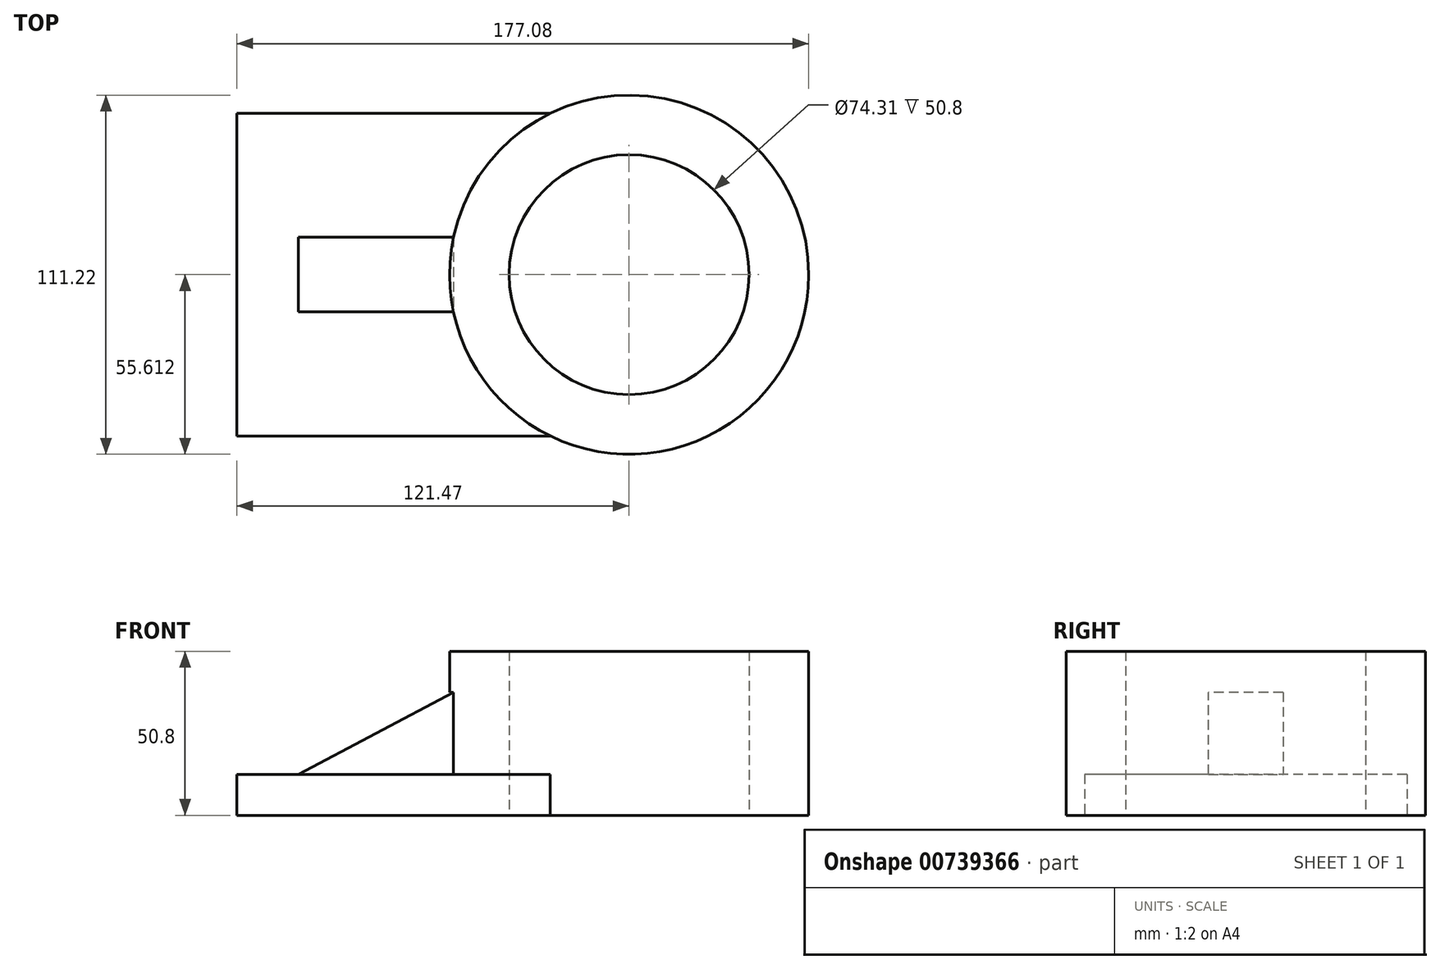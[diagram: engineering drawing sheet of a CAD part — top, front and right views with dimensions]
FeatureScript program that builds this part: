
annotation { "Feature Type Name" : "Feature", "Feature Type Description" : "" }
export const myFeature = defineFeature(function(context is Context, id is Id, definition is map)
    precondition{}
    {
        {
            var Q0;
            Q0=qCreatedBy(makeId("Top.planeOp"),FACE);
            var sketch = newSketch(context, id + "F0", { "sketchPlane" : qUnion([Q0])});
            skLineSegment(sketch, "E0.bottom", {"start": v(-73.9, 65.56) * mm, "end": v(23.08, 65.56) * mm});
            skLineSegment(sketch, "E0.top", {"start": v(-73.9, -34.3) * mm, "end": v(23.08, -34.3) * mm});
            skLineSegment(sketch, "E0.left", {"start": v(-73.9, 65.56) * mm, "end": v(-73.9, -34.3) * mm});
            skCircle(sketch, "E1", {"center": v(47.56, 15.63) * mm, "radius": 55.6 * mm});
            skPoint(sketch, "E1.third.point", {"position": v(92.68, -16.87) * mm});
            skCircle(sketch, "E2", {"center": v(47.56, 15.63) * mm, "radius": 37.16 * mm});
            skSolve(sketch);
        }
        {
            var Q0;
            {var subQ0=sQuery(id+"F0.wireOp",EDGE,"E0.bottom");Q0=makeQuery(id+"F0.imprint","IMPRINT",FACE,{"disambiguationData":[TD([[makeQuery(id+"F0.imprint","IMPRINT",EDGE,{"derivedFrom":subQ0}),-1.0]])]});}
            extrude(context, id + "F1", {"entities" : qUnion([Q0]), "depth" : 12.7 * mm, "offsetDistance" : 25.4 * mm});
        }
        {
            var Q0;
            Q0=makeQuery(id+"F0.imprint","IMPRINT",FACE,{"disambiguationData":[TD([[makeQuery(id+"F0.imprint","IMPRINT",EDGE,{"derivedFrom":sQuery(id+"F0.wireOp",EDGE,"E2")}),-1.0]])]});
            extrude(context, id + "F2", {"entities" : qUnion([Q0]), "operationType" : NewBodyOperationType.ADD, "depth" : 50.8 * mm, "offsetDistance" : 25.4 * mm});
        }
        {
            var Q0;
            Q0=qCreatedBy(makeId("Top.planeOp"),FACE);
            var sketch = newSketch(context, id + "F3", { "sketchPlane" : qUnion([Q0])});
            skLineSegment(sketch, "E3.bottom", {"start": v(-54.86, 27.24) * mm, "end": v(7.6, 27.24) * mm});
            skLineSegment(sketch, "E3.top", {"start": v(-54.86, 4.08) * mm, "end": v(7.6, 4.08) * mm});
            skLineSegment(sketch, "E3.left", {"start": v(-54.86, 27.24) * mm, "end": v(-54.86, 4.08) * mm});
            skLineSegment(sketch, "E3.right", {"start": v(7.6, 27.24) * mm, "end": v(7.6, 4.08) * mm});
            skSolve(sketch);
        }
        {
            var Q0;
            Q0=makeQuery(id+"F3.imprint","IMPRINT",FACE,{"disambiguationData":[TD([[makeQuery(id+"F3.imprint","IMPRINT",EDGE,{"derivedFrom":sQuery(id+"F3.wireOp",EDGE,"E3.bottom")}),-1.0]])]});
            extrude(context, id + "F4", {"entities" : qUnion([Q0]), "operationType" : NewBodyOperationType.ADD, "depth" : 38.1 * mm, "offsetDistance" : 25.4 * mm});
        }
        {
            var Q0;
            Q0=makeQuery(id+"F4.opExtrude","SWEPT_FACE",FACE,{"disambiguationData":[OSD([sQuery(id+"F3.wireOp",EDGE,"E3.top")])]});
            var sketch = newSketch(context, id + "F5", { "sketchPlane" : qUnion([Q0])});
            skLineSegment(sketch, "E4", {"start": v(-54.86, 12.7) * mm, "end": v(-6.83, 38.1) * mm});
            skLineSegment(sketch, "E5", {"start": v(-6.83, 38.1) * mm, "end": v(-54.86, 38.1) * mm});
            skLineSegment(sketch, "E6", {"start": v(-54.86, 38.1) * mm, "end": v(-54.86, 12.7) * mm});
            skSolve(sketch);
        }
        {
            var Q0;
            Q0=makeQuery(id+"F5.imprint","IMPRINT",FACE,{"disambiguationData":[TD([[makeQuery(id+"F5.imprint","IMPRINT",EDGE,{"derivedFrom":sQuery(id+"F5.wireOp",EDGE,"E4")}),1.0]])]});
            extrude(context, id + "F6", {"entities" : qUnion([Q0]), "operationType" : NewBodyOperationType.REMOVE, "oppositeDirection" : true, "depth" : 25.4 * mm, "offsetDistance" : 25.4 * mm});
        }
    });
